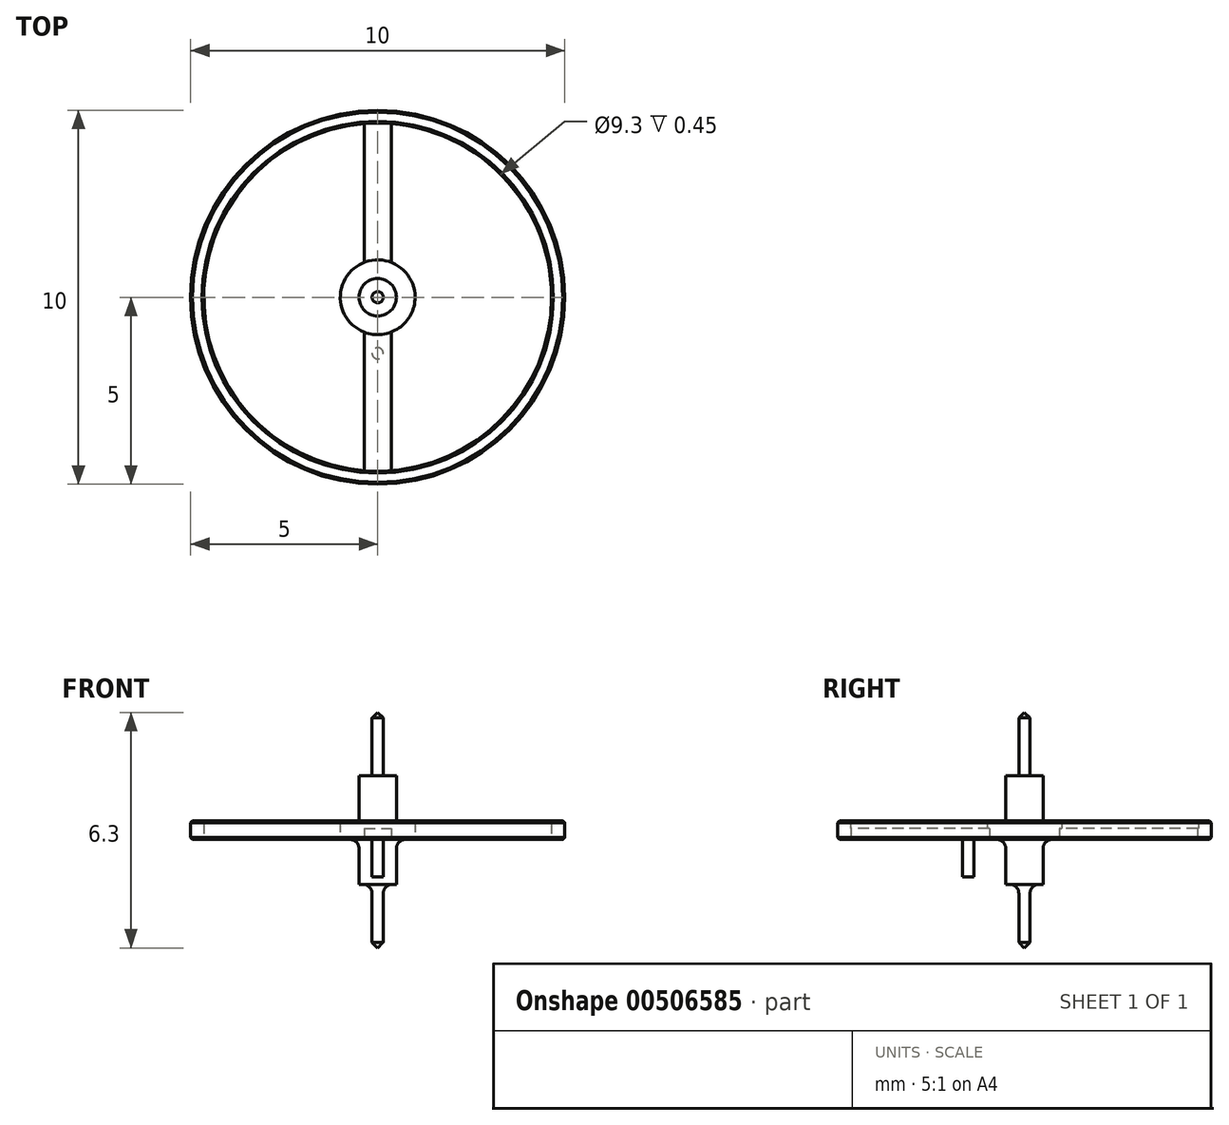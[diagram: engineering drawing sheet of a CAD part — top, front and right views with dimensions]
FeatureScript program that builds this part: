
annotation { "Feature Type Name" : "Feature", "Feature Type Description" : "" }
export const myFeature = defineFeature(function(context is Context, id is Id, definition is map)
    precondition{}
    {
        {
            var Q0;
            Q0=qCreatedBy(makeId("Top.planeOp"),FACE);
            var sketch = newSketch(context, id + "F0", { "sketchPlane" : qUnion([Q0])});
            skCircle(sketch, "E0", {"center": v(0, 0) * mm, "radius": 5 * mm});
            skCircle(sketch, "E1", {"center": v(0, 0) * mm, "radius": 4.65 * mm});
            skCircle(sketch, "E2", {"center": v(0, 0) * mm, "radius": 1 * mm});
            skCircle(sketch, "E3", {"center": v(0, 0) * mm, "radius": 0.5 * mm});
            skCircle(sketch, "E4", {"center": v(0, 0) * mm, "radius": 0.15 * mm});
            skSolve(sketch);
        }
        {
            var Q0;
            Q0=makeQuery(id+"F0.imprint","IMPRINT",FACE,{"disambiguationData":[TD([[makeQuery(id+"F0.imprint","IMPRINT",EDGE,{"derivedFrom":sQuery(id+"F0.wireOp",EDGE,"E0")}),1.0]])]});
            var Q1;
            Q1=makeQuery(id+"F0.imprint","IMPRINT",FACE,{"disambiguationData":[TD([[makeQuery(id+"F0.imprint","IMPRINT",EDGE,{"derivedFrom":sQuery(id+"F0.wireOp",EDGE,"E2")}),1.0]])]});
            extrude(context, id + "F1", {"entities" : qUnion([Q0, Q1]), "depth" : 0.5 * mm});
        }
        {
            var Q0;
            Q0=makeQuery(id+"F0.imprint","IMPRINT",FACE,{"disambiguationData":[TD([[makeQuery(id+"F0.imprint","IMPRINT",EDGE,{"derivedFrom":sQuery(id+"F0.wireOp",EDGE,"E3")}),1.0]])]});
            extrude(context, id + "F2", {"entities" : qUnion([Q0]), "operationType" : NewBodyOperationType.ADD, "depth" : 1.7 * mm, "hasSecondDirection" : true, "secondDirectionOppositeDirection" : true, "secondDirectionDepth" : 1.2 * mm});
        }
        {
            var Q0;
            Q0=makeQuery(id+"F0.imprint","IMPRINT",FACE,{"disambiguationData":[TD([[makeQuery(id+"F0.imprint","IMPRINT",EDGE,{"derivedFrom":sQuery(id+"F0.wireOp",EDGE,"E4")}),1.0]])]});
            extrude(context, id + "F3", {"entities" : qUnion([Q0]), "operationType" : NewBodyOperationType.ADD, "depth" : 3.4 * mm, "hasSecondDirection" : true, "secondDirectionOppositeDirection" : true, "secondDirectionDepth" : 2.9 * mm});
        }
        {
            var Q0;
            Q0=makeQuery(id+"F0.imprint","IMPRINT",FACE,{"disambiguationData":[TD([[makeQuery(id+"F0.imprint","IMPRINT",EDGE,{"derivedFrom":sQuery(id+"F0.wireOp",EDGE,"E1")}),1.0]])]});
            var sketch = newSketch(context, id + "F4", { "sketchPlane" : qUnion([Q0])});
            skLineSegment(sketch, "E5.bottom", {"start": v(-0.36, 4.74) * mm, "end": v(0.36, 4.74) * mm});
            skLineSegment(sketch, "E5.top", {"start": v(-0.36, -4.74) * mm, "end": v(0.36, -4.74) * mm});
            skLineSegment(sketch, "E5.left", {"start": v(-0.36, 4.74) * mm, "end": v(-0.36, -4.74) * mm});
            skLineSegment(sketch, "E5.right", {"start": v(0.36, 4.74) * mm, "end": v(0.36, -4.74) * mm});
            skPoint(sketch, "E5.middle", {"position": v(0, 0) * mm});
            skSolve(sketch);
        }
        {
            var Q0;
            {var subQ0=sQuery(id+"F4.wireOp",EDGE,"E5.left");var subQ1=makeQuery(id+"F0.imprint","IMPRINT",EDGE,{"derivedFrom":sQuery(id+"F0.wireOp",EDGE,"E1")});var subQ2=makeQuery(id+"F4.imprint","INTERSECT",VERTEX,{"disambiguationData":[OD(1.0)],"derivedFrom":[subQ1,subQ0]});Q0=makeQuery(id+"F4.imprint","IMPRINT",FACE,{"disambiguationData":[TD([[makeQuery(id+"F4.imprint","IMPRINT",EDGE,{"disambiguationData":[TD([[subQ2,1.0]])],"derivedFrom":subQ0}),1.0]])]});}
            var Q1;
            {var subQ0=sQuery(id+"F4.wireOp",EDGE,"E5.left");var subQ1=makeQuery(id+"F0.imprint","IMPRINT",EDGE,{"derivedFrom":sQuery(id+"F0.wireOp",EDGE,"E1")});var subQ2=makeQuery(id+"F4.imprint","INTERSECT",VERTEX,{"disambiguationData":[OD(0.0)],"derivedFrom":[subQ1,subQ0]});Q1=makeQuery(id+"F4.imprint","IMPRINT",FACE,{"disambiguationData":[TD([[makeQuery(id+"F4.imprint","IMPRINT",EDGE,{"disambiguationData":[TD([[subQ2,-1.0]])],"derivedFrom":subQ0}),1.0]])]});}
            extrude(context, id + "F5", {"entities" : qUnion([Q0, Q1]), "operationType" : NewBodyOperationType.ADD, "depth" : 0.3 * mm});
        }
        {
            var Q0;
            Q0=makeQuery(id+"F1.opExtrude","CAP_EDGE",EDGE,{"disambiguationData":[OSD([sQuery(id+"F0.wireOp",EDGE,"E3")])],"isStart":false});
            var Q1;
            Q1=makeQuery(id+"F1.opExtrude","CAP_EDGE",EDGE,{"disambiguationData":[OSD([sQuery(id+"F0.wireOp",EDGE,"E3")])],"isStart":true});
            var Q2;
            Q2=makeQuery(id+"F2.opExtrude","CAP_EDGE",EDGE,{"disambiguationData":[OSD([sQuery(id+"F0.wireOp",EDGE,"E4")])],"isStart":true});
            var Q3;
            Q3=makeQuery(id+"F2.opExtrude","CAP_EDGE",EDGE,{"disambiguationData":[OSD([sQuery(id+"F0.wireOp",EDGE,"E4")])],"isStart":false});
            fillet(context, id + "F6", {"entities" : qUnion([Q0, Q1, Q2, Q3]), "radius" : 0.24 * mm, "tangentPropagation" : true, "allowEdgeOverflow" : false});
        }
        {
            var Q0;
            Q0=makeQuery(id+"F1.opExtrude","CAP_EDGE",EDGE,{"disambiguationData":[OSD([sQuery(id+"F0.wireOp",EDGE,"E0")])],"isStart":false});
            var Q1;
            Q1=makeQuery(id+"F1.opExtrude","CAP_EDGE",EDGE,{"disambiguationData":[OSD([sQuery(id+"F0.wireOp",EDGE,"E1")])],"isStart":false});
            var Q2;
            {var subQ0=sQuery(id+"F4.wireOp",EDGE,"E5.left");var subQ1=sQuery(id+"F0.wireOp",EDGE,"E1");var subQ2=makeQuery(id+"F0.imprint","IMPRINT",EDGE,{"derivedFrom":subQ1});var subQ3=makeQuery(id+"F4.imprint","INTERSECT",VERTEX,{"disambiguationData":[OD(0.0)],"derivedFrom":[subQ2,subQ0]});var subQ7=makeQuery(id+"F4.imprint","IMPRINT",EDGE,{"disambiguationData":[TD([[subQ3,-1.0]])],"derivedFrom":subQ0});Q2=makeQuery(id+"F5.boolean.opBoolean","SPLIT",EDGE,{"disambiguationData":[TD([makeQuery(id+"F5.opExtrude","SWEPT_FACE",FACE,{"disambiguationData":[OSD([subQ0]),TDD([subQ7])]})])],"derivedFrom":makeQuery(id+"F1.opExtrude","CAP_EDGE",EDGE,{"disambiguationData":[OSD([subQ1])],"isStart":true})});}
            var Q3;
            Q3=makeQuery(id+"F1.opExtrude","CAP_EDGE",EDGE,{"disambiguationData":[OSD([sQuery(id+"F0.wireOp",EDGE,"E0")])],"isStart":true});
            chamfer(context, id + "F7", {"entities" : qUnion([Q0, Q1, Q2, Q3]), "width" : 0.05 * mm, "tangentPropagation" : true});
        }
        {
            var Q0;
            Q0=makeQuery(id+"F3.opExtrude","CAP_EDGE",EDGE,{"disambiguationData":[OSD([sQuery(id+"F0.wireOp",EDGE,"E4")])],"isStart":false});
            var Q1;
            Q1=makeQuery(id+"F3.opExtrude","CAP_EDGE",EDGE,{"disambiguationData":[OSD([sQuery(id+"F0.wireOp",EDGE,"E4")])],"isStart":true});
            chamfer(context, id + "F8", {"entities" : qUnion([Q0, Q1]), "width" : 0.15 * mm, "tangentPropagation" : true});
        }
        {
            var Q0;
            Q0=makeQuery(id+"F0.imprint","IMPRINT",FACE,{"disambiguationData":[TD([[makeQuery(id+"F0.imprint","IMPRINT",EDGE,{"derivedFrom":sQuery(id+"F0.wireOp",EDGE,"E1")}),1.0]])]});
            var sketch = newSketch(context, id + "F9", { "sketchPlane" : qUnion([Q0])});
            skCircle(sketch, "E6", {"center": v(0, -1.5) * mm, "radius": 0.15 * mm});
            skSolve(sketch);
        }
        {
            var Q0;
            Q0 = qSketchRegion(id + "F9", true);
            var Q1;
            Q1=sQuery(id+"F9.wireOp",EDGE,"E6");
            extrude(context, id + "F10", {"entities" : qUnion([Q0]), "operationType" : NewBodyOperationType.ADD, "surfaceEntities" : qUnion([Q1]), "depth" : -1 * mm});
        }
    });
